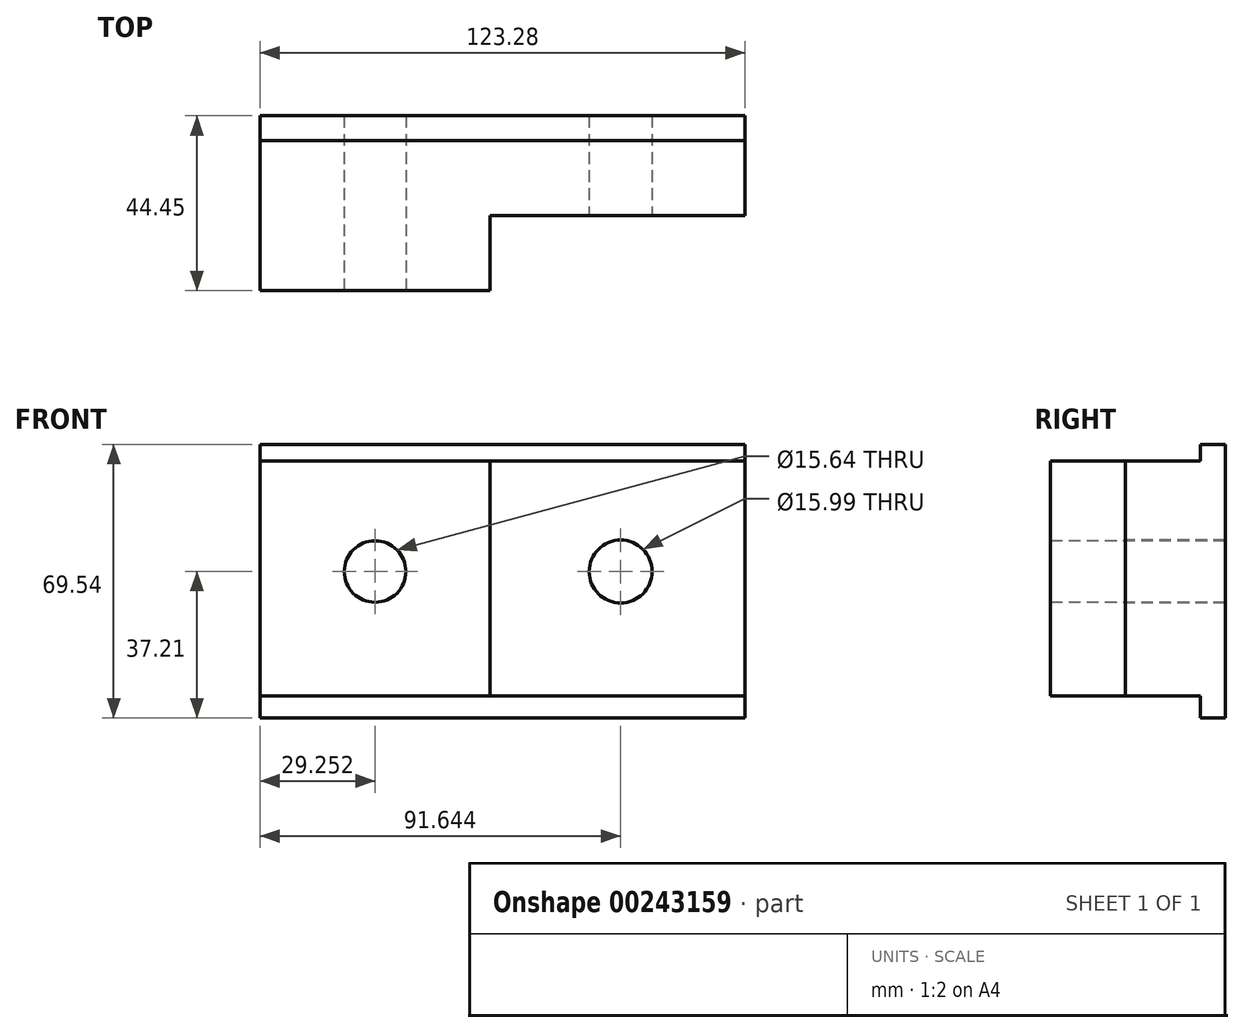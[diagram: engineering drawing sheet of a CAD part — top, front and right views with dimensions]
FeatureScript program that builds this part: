
annotation { "Feature Type Name" : "Feature", "Feature Type Description" : "" }
export const myFeature = defineFeature(function(context is Context, id is Id, definition is map)
    precondition{}
    {
        {
            var Q0;
            Q0=qCreatedBy(makeId("Front.planeOp"),FACE);
            var sketch = newSketch(context, id + "F0", { "sketchPlane" : qUnion([Q0])});
            skLineSegment(sketch, "E0.bottom", {"start": v(-58.5, 32.33) * mm, "end": v(64.78, 32.33) * mm});
            skLineSegment(sketch, "E0.top", {"start": v(-58.5, -37.21) * mm, "end": v(64.78, -37.21) * mm});
            skLineSegment(sketch, "E0.left", {"start": v(-58.5, 32.33) * mm, "end": v(-58.5, -37.21) * mm});
            skLineSegment(sketch, "E0.right", {"start": v(64.78, 32.33) * mm, "end": v(64.78, -37.21) * mm});
            skSolve(sketch);
        }
        {
            var Q0;
            Q0 = qSketchRegion(id + "F0", true);
            extrude(context, id + "F1", {"entities" : qUnion([Q0]), "depth" : 25.4 * mm});
        }
        {
            var Q0;
            Q0=makeQuery(id+"F1.opExtrude","CAP_FACE",FACE,{"disambiguationData":[OSD([sQuery(id+"F0.wireOp",EDGE,"E0.bottom"),sQuery(id+"F0.wireOp",EDGE,"E0.top"),sQuery(id+"F0.wireOp",EDGE,"E0.left"),sQuery(id+"F0.wireOp",EDGE,"E0.right")])],"isStart":false});
            var sketch = newSketch(context, id + "F2", { "sketchPlane" : qUnion([Q0])});
            skLineSegment(sketch, "E1", {"start": v(64.78, -31.63) * mm, "end": v(-58.5, -31.63) * mm});
            skLineSegment(sketch, "E2", {"start": v(-58.5, 28.14) * mm, "end": v(64.78, 28.14) * mm});
            skSolve(sketch);
        }
        {
            var Q0;
            {var subQ0=sQuery(id+"F2.wireOp",EDGE,"E2");Q0=makeQuery(id+"F2.imprint","IMPRINT",FACE,{"disambiguationData":[TD([[makeQuery(id+"F2.imprint","IMPRINT",EDGE,{"derivedFrom":subQ0}),1.0]])]});}
            var Q1;
            {var subQ0=sQuery(id+"F2.wireOp",EDGE,"E1");Q1=makeQuery(id+"F2.imprint","IMPRINT",FACE,{"disambiguationData":[TD([[makeQuery(id+"F2.imprint","IMPRINT",EDGE,{"derivedFrom":subQ0}),1.0]])]});}
            extrude(context, id + "F3", {"entities" : qUnion([Q0, Q1]), "operationType" : NewBodyOperationType.REMOVE, "oppositeDirection" : true, "depth" : 19.05 * mm});
        }
        {
            var Q0;
            Q0=makeQuery(id+"F1.opExtrude","CAP_FACE",FACE,{"disambiguationData":[OSD([sQuery(id+"F0.wireOp",EDGE,"E0.bottom"),sQuery(id+"F0.wireOp",EDGE,"E0.top"),sQuery(id+"F0.wireOp",EDGE,"E0.left"),sQuery(id+"F0.wireOp",EDGE,"E0.right")])],"isStart":false});
            var sketch = newSketch(context, id + "F4", { "sketchPlane" : qUnion([Q0])});
            skLineSegment(sketch, "E3", {"start": v(0, 28.14) * mm, "end": v(0, -31.63) * mm});
            skSolve(sketch);
        }
        {
            var Q0;
            {var subQ0=sQuery(id+"F4.wireOp",EDGE,"E3");Q0=makeQuery(id+"F4.imprint","IMPRINT",FACE,{"disambiguationData":[TD([[makeQuery(id+"F4.imprint","IMPRINT",EDGE,{"derivedFrom":subQ0}),-1.0]])]});}
            extrude(context, id + "F5", {"entities" : qUnion([Q0]), "operationType" : NewBodyOperationType.ADD, "depth" : 19.05 * mm});
        }
        {
            var Q0;
            Q0=makeQuery(id+"F5.opExtrude","CAP_FACE",FACE,{"disambiguationData":[OSD([sQuery(id+"F0.wireOp",EDGE,"E0.left"),sQuery(id+"F2.wireOp",EDGE,"E1"),sQuery(id+"F2.wireOp",EDGE,"E2"),sQuery(id+"F4.wireOp",EDGE,"E3")])],"isStart":false});
            var sketch = newSketch(context, id + "F6", { "sketchPlane" : qUnion([Q0])});
            skCircle(sketch, "E4", {"center": v(-29.25, 0) * mm, "radius": 7.82 * mm});
            skPoint(sketch, "E4.centerSnap0", {"position": v(-29.25, 28.14) * mm});
            skSolve(sketch);
        }
        {
            var Q0;
            Q0=makeQuery(id+"F6.imprint","IMPRINT",FACE,{"disambiguationData":[TD([[makeQuery(id+"F6.imprint","IMPRINT",EDGE,{"derivedFrom":sQuery(id+"F6.wireOp",EDGE,"E4")}),1.0]])]});
            extrude(context, id + "F7", {"entities" : qUnion([Q0]), "operationType" : NewBodyOperationType.REMOVE, "oppositeDirection" : true, "depth" : 84.84 * mm});
        }
        {
            var Q0;
            Q0=makeQuery(id+"F1.opExtrude","CAP_FACE",FACE,{"disambiguationData":[OSD([sQuery(id+"F0.wireOp",EDGE,"E0.bottom"),sQuery(id+"F0.wireOp",EDGE,"E0.top"),sQuery(id+"F0.wireOp",EDGE,"E0.left"),sQuery(id+"F0.wireOp",EDGE,"E0.right")])],"isStart":false});
            var sketch = newSketch(context, id + "F8", { "sketchPlane" : qUnion([Q0])});
            skCircle(sketch, "E5", {"center": v(33.14, 0) * mm, "radius": 8 * mm});
            skSolve(sketch);
        }
        {
            var Q0;
            Q0 = qSketchRegion(id + "F8", true);
            extrude(context, id + "F9", {"entities" : qUnion([Q0]), "operationType" : NewBodyOperationType.REMOVE, "oppositeDirection" : true, "depth" : 31.24 * mm});
        }
    });
